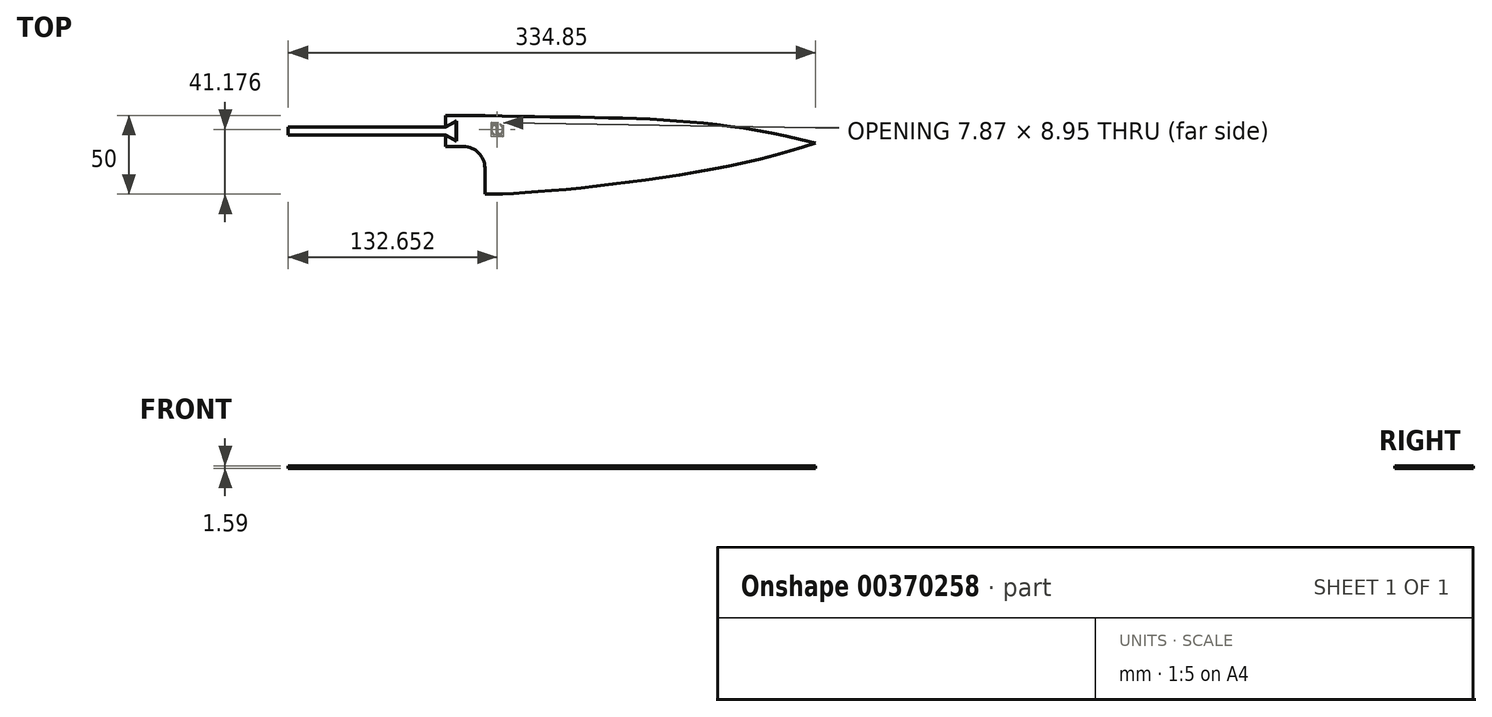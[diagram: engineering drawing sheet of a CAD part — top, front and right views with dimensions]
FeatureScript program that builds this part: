
annotation { "Feature Type Name" : "Feature", "Feature Type Description" : "" }
export const myFeature = defineFeature(function(context is Context, id is Id, definition is map)
    precondition{}
    {
        {
            var Q0;
            Q0=qCreatedBy(makeId("Top.planeOp"),FACE);
            var sketch = newSketch(context, id + "F0", { "sketchPlane" : qUnion([Q0])});
            skLineSegment(sketch, "E0.left", {"start": v(-105, -8.25) * mm, "end": v(-105, -25) * mm});
            skFitSpline(sketch, "E1", {"points": [v(-105, 25) * mm, v(105, 7.62) * mm, v(143.33, 2.67) * mm], "startDerivative": vector(362.44, -9.56) * mm, "endDerivative": vector(-287.35, 150.52) * mm});
            skFitSpline(sketch, "E2", {"points": [v(-105, -25) * mm, v(105, 7.62) * mm], "startDerivative": vector(110.44, 0) * mm, "endDerivative": vector(175.52, 63.31) * mm});
            skArc(sketch, "E3", {"start": v(-105, -8.25) * mm, "mid": v(-108.95, 1.3) * mm, "end": v(-118.5, 5.25) * mm});
            skLineSegment(sketch, "E4", {"start": v(-105, -25) * mm, "end": v(-105, -8.25) * mm});
            skLineSegment(sketch, "E5", {"start": v(-118.5, 5.25) * mm, "end": v(-123.5, 5.25) * mm});
            skLineSegment(sketch, "E6", {"start": v(-105, 25) * mm, "end": v(-123.5, 25) * mm});
            skLineSegment(sketch, "E7.bottom", {"start": v(-123.5, 25) * mm, "end": v(-129.85, 25) * mm});
            skLineSegment(sketch, "E7.top", {"start": v(-123.5, 5.25) * mm, "end": v(-129.85, 5.25) * mm});
            skLineSegment(sketch, "E7.right", {"start": v(-129.85, 25) * mm, "end": v(-129.85, 17.62) * mm});
            skLineSegment(sketch, "E8.bottom", {"start": v(-229.85, 17.62) * mm, "end": v(-129.85, 17.62) * mm});
            skLineSegment(sketch, "E8.top", {"start": v(-229.85, 12.62) * mm, "end": v(-129.85, 12.62) * mm});
            skLineSegment(sketch, "E8.left", {"start": v(-229.85, 17.62) * mm, "end": v(-229.85, 12.62) * mm});
            skLineSegment(sketch, "E9.trimOffspring", {"start": v(-129.85, 12.62) * mm, "end": v(-129.85, 5.25) * mm});
            skSolve(sketch);
        }
        {
            var Q0;
            Q0 = qSketchRegion(id + "F0", true);
            extrude(context, id + "F1", {"entities" : qUnion([Q0]), "depth" : 1.59 * mm});
        }
        {
            var Q0;
            Q0=makeQuery(id+"F1.opExtrude","CAP_FACE",FACE,{"disambiguationData":[OSD([sQuery(id+"F0.wireOp",EDGE,"E1"),sQuery(id+"F0.wireOp",EDGE,"E2"),sQuery(id+"F0.wireOp",EDGE,"E3"),sQuery(id+"F0.wireOp",EDGE,"E4"),sQuery(id+"F0.wireOp",EDGE,"E5"),sQuery(id+"F0.wireOp",EDGE,"E6"),sQuery(id+"F0.wireOp",EDGE,"E7.bottom"),sQuery(id+"F0.wireOp",EDGE,"E7.top"),sQuery(id+"F0.wireOp",EDGE,"E7.right"),sQuery(id+"F0.wireOp",EDGE,"E8.bottom"),sQuery(id+"F0.wireOp",EDGE,"E8.top"),sQuery(id+"F0.wireOp",EDGE,"E8.left"),sQuery(id+"F0.wireOp",EDGE,"E9.trimOffspring")])],"isStart":true});
            var sketch = newSketch(context, id + "F2", { "sketchPlane" : qUnion([Q0])});
            skArc(sketch, "E10", {"start": v(-95.06, -12.8) * mm, "mid": v(-100.52, -13.94) * mm, "end": v(-99.53, -19.43) * mm});
            skArc(sketch, "E11", {"start": v(-95.53, -13.1) * mm, "mid": v(-96.22, -12.82) * mm, "end": v(-96.95, -12.68) * mm});
            skLineSegment(sketch, "E12", {"start": v(-97.45, -12.68) * mm, "end": v(-97.45, -17.8) * mm});
            skLineSegment(sketch, "E13", {"start": v(-96.95, -12.68) * mm, "end": v(-96.95, -13.98) * mm});
            skLineSegment(sketch, "E14", {"start": v(-93.3, -11.7) * mm, "end": v(-94.87, -12.92) * mm});
            skLineSegment(sketch, "E15", {"start": v(-97.45, -17.8) * mm, "end": v(-99.11, -19.1) * mm});
            skPoint(sketch, "E16.orphan", {"position": v(-97.2, -12.18) * mm});
            skLineSegment(sketch, "E17.trimOffspring", {"start": v(-95.06, -12.8) * mm, "end": v(-93.3, -11.7) * mm});
            skLineSegment(sketch, "E18.trimOffspring", {"start": v(-95.28, -13.25) * mm, "end": v(-96.95, -14.56) * mm});
            skLineSegment(sketch, "E19.trimOffspring", {"start": v(-96.95, -14.56) * mm, "end": v(-96.95, -19.67) * mm});
            skLineSegment(sketch, "E20.trimOffspring", {"start": v(-96.95, -13.98) * mm, "end": v(-95.53, -13.1) * mm});
            skArc(sketch, "E21.trimOffspring", {"start": v(-97.45, -12.68) * mm, "mid": v(-100.59, -15.3) * mm, "end": v(-99.11, -19.1) * mm});
            skPoint(sketch, "E22.orphan", {"position": v(-97.2, -14.43) * mm});
            skLineSegment(sketch, "E23.trimOffspring", {"start": v(-97.45, -18.37) * mm, "end": v(-97.45, -19.67) * mm});
            skPoint(sketch, "E24.orphan", {"position": v(-97.2, -17.93) * mm});
            skLineSegment(sketch, "E25.trimOffspring", {"start": v(-97.45, -18.37) * mm, "end": v(-98.86, -19.25) * mm});
            skArc(sketch, "E26.trimOffspring", {"start": v(-96.95, -19.67) * mm, "mid": v(-93.81, -17.06) * mm, "end": v(-95.28, -13.25) * mm});
            skArc(sketch, "E27.trimOffspring", {"start": v(-98.86, -19.25) * mm, "mid": v(-98.18, -19.54) * mm, "end": v(-97.45, -19.67) * mm});
            skArc(sketch, "E28.trimOffspring", {"start": v(-99.34, -19.55) * mm, "mid": v(-93.88, -18.41) * mm, "end": v(-94.87, -12.92) * mm});
            skLineSegment(sketch, "E29.trimOffspring", {"start": v(-99.34, -19.55) * mm, "end": v(-101.09, -20.65) * mm});
            skLineSegment(sketch, "E30.trimOffspring", {"start": v(-99.53, -19.43) * mm, "end": v(-101.09, -20.65) * mm});
            skSolve(sketch);
        }
        {
            var Q0;
            Q0 = qSketchRegion(id + "F2", true);
            extrude(context, id + "F3", {"entities" : qUnion([Q0]), "operationType" : NewBodyOperationType.REMOVE, "oppositeDirection" : true, "offsetDistance" : 25.4 * mm, "depth" : .75 * mm, "hasDraft" : true, "draftAngle" : 20 * degree, "draftPullDirection" : true});
        }
        {
            var Q0;
            Q0=makeQuery(id+"F1.opExtrude","SWEPT_BODY",BODY,{"disambiguationData":[OSD([sQuery(id+"F0.wireOp",EDGE,"E1"),sQuery(id+"F0.wireOp",EDGE,"E2"),sQuery(id+"F0.wireOp",EDGE,"E3"),sQuery(id+"F0.wireOp",EDGE,"E4"),sQuery(id+"F0.wireOp",EDGE,"E5"),sQuery(id+"F0.wireOp",EDGE,"E6"),sQuery(id+"F0.wireOp",EDGE,"E7.bottom"),sQuery(id+"F0.wireOp",EDGE,"E7.top"),sQuery(id+"F0.wireOp",EDGE,"E7.right"),sQuery(id+"F0.wireOp",EDGE,"E8.bottom"),sQuery(id+"F0.wireOp",EDGE,"E8.top"),sQuery(id+"F0.wireOp",EDGE,"E8.left"),sQuery(id+"F0.wireOp",EDGE,"E9.trimOffspring")])]});
            transform(context, id + "F4", {"entities" : qUnion([Q0]), "transformType" : TransformType.TRANSLATION_3D, "dx" : 0 * mm, "dy" : 0 * mm, "dz" : 0 * mm, "makeCopy" : true});
        }
        {
            var Q0;
            {var subQ0=sQuery(id+"F0.wireOp",EDGE,"E8.top");var subQ1=sQuery(id+"F0.wireOp",EDGE,"E8.bottom");var subQ2=sQuery(id+"F0.wireOp",EDGE,"E7.right");var subQ3=sQuery(id+"F0.wireOp",EDGE,"E7.bottom");var subQ4=sQuery(id+"F0.wireOp",EDGE,"E6");var subQ5=sQuery(id+"F0.wireOp",EDGE,"E7.top");var subQ6=sQuery(id+"F0.wireOp",EDGE,"E5");var subQ7=sQuery(id+"F0.wireOp",EDGE,"E8.left");var subQ8=sQuery(id+"F0.wireOp",EDGE,"E1");var subQ9=sQuery(id+"F0.wireOp",EDGE,"E4");var subQ10=sQuery(id+"F0.wireOp",EDGE,"E2");var subQ11=sQuery(id+"F0.wireOp",EDGE,"E3");var subQ12=sQuery(id+"F0.wireOp",EDGE,"E9.trimOffspring");Q0=makeQuery(id+"F4.opPattern","COPY",FACE,{"derivedFrom":makeQuery(id+"F3.boolean.opBoolean","SPLIT",FACE,{"disambiguationData":[TD([makeQuery(id+"F1.opExtrude","SWEPT_FACE",FACE,{"disambiguationData":[OSD([subQ8])]})])],"derivedFrom":makeQuery(id+"F1.opExtrude","CAP_FACE",FACE,{"disambiguationData":[OSD([subQ8,subQ10,subQ11,subQ9,subQ6,subQ4,subQ3,subQ5,subQ2,subQ1,subQ0,subQ7,subQ12])],"isStart":true})}),"instanceName":"1"});}
            var sketch = newSketch(context, id + "F5", { "sketchPlane" : qUnion([Q0])});
            skLineSegment(sketch, "E31", {"start": v(-129.85, -17.62) * mm, "end": v(-123.18, -21.47) * mm});
            skLineSegment(sketch, "E32", {"start": v(-123.18, -21.47) * mm, "end": v(-123.18, -8.77) * mm});
            skLineSegment(sketch, "E33", {"start": v(-123.18, -8.77) * mm, "end": v(-129.85, -12.62) * mm});
            skLineSegment(sketch, "E34.0", {"start": v(-123.12, -8.66) * mm, "end": v(-129.85, -12.55) * mm});
            skLineSegment(sketch, "E34.1", {"start": v(-123.12, -21.58) * mm, "end": v(-123.12, -8.66) * mm});
            skLineSegment(sketch, "E34.2", {"start": v(-129.85, -17.7) * mm, "end": v(-123.12, -21.58) * mm});
            skLineSegment(sketch, "E35", {"start": v(-129.85, -12.62) * mm, "end": v(-129.85, -12.55) * mm});
            skLineSegment(sketch, "E36", {"start": v(-129.85, -17.62) * mm, "end": v(-129.85, -17.7) * mm});
            skSolve(sketch);
        }
        {
            var Q0;
            Q0=makeQuery(id+"F4.opPattern","COPY",FACE,{"derivedFrom":makeQuery(id+"F3.boolean.opBoolean","SPLIT",FACE,{"disambiguationData":[TD([makeQuery(id+"F3.opExtrude","SWEPT_FACE",FACE,{"disambiguationData":[OSD([sQuery(id+"F2.wireOp",EDGE,"E18.trimOffspring")])]})])],"derivedFrom":makeQuery(id+"F1.opExtrude","CAP_FACE",FACE,{"disambiguationData":[OSD([sQuery(id+"F0.wireOp",EDGE,"E1"),sQuery(id+"F0.wireOp",EDGE,"E2"),sQuery(id+"F0.wireOp",EDGE,"E3"),sQuery(id+"F0.wireOp",EDGE,"E4"),sQuery(id+"F0.wireOp",EDGE,"E5"),sQuery(id+"F0.wireOp",EDGE,"E6"),sQuery(id+"F0.wireOp",EDGE,"E7.bottom"),sQuery(id+"F0.wireOp",EDGE,"E7.top"),sQuery(id+"F0.wireOp",EDGE,"E7.right"),sQuery(id+"F0.wireOp",EDGE,"E8.bottom"),sQuery(id+"F0.wireOp",EDGE,"E8.top"),sQuery(id+"F0.wireOp",EDGE,"E8.left"),sQuery(id+"F0.wireOp",EDGE,"E9.trimOffspring")])],"isStart":true})}),"instanceName":"1"});
            var Q1;
            Q1=makeQuery(id+"F4.opPattern","COPY",FACE,{"derivedFrom":makeQuery(id+"F3.boolean.opBoolean","SPLIT",FACE,{"disambiguationData":[TD([makeQuery(id+"F3.opExtrude","SWEPT_FACE",FACE,{"disambiguationData":[OSD([sQuery(id+"F2.wireOp",EDGE,"E25.trimOffspring")])]})])],"derivedFrom":makeQuery(id+"F1.opExtrude","CAP_FACE",FACE,{"disambiguationData":[OSD([sQuery(id+"F0.wireOp",EDGE,"E1"),sQuery(id+"F0.wireOp",EDGE,"E2"),sQuery(id+"F0.wireOp",EDGE,"E3"),sQuery(id+"F0.wireOp",EDGE,"E4"),sQuery(id+"F0.wireOp",EDGE,"E5"),sQuery(id+"F0.wireOp",EDGE,"E6"),sQuery(id+"F0.wireOp",EDGE,"E7.bottom"),sQuery(id+"F0.wireOp",EDGE,"E7.top"),sQuery(id+"F0.wireOp",EDGE,"E7.right"),sQuery(id+"F0.wireOp",EDGE,"E8.bottom"),sQuery(id+"F0.wireOp",EDGE,"E8.top"),sQuery(id+"F0.wireOp",EDGE,"E8.left"),sQuery(id+"F0.wireOp",EDGE,"E9.trimOffspring")])],"isStart":true})}),"instanceName":"1"});
            var Q2;
            Q2=makeQuery(id+"F4.opPattern","COPY",FACE,{"derivedFrom":makeQuery(id+"F3.boolean.opBoolean","SPLIT",FACE,{"disambiguationData":[TD([makeQuery(id+"F3.opExtrude","SWEPT_FACE",FACE,{"disambiguationData":[OSD([sQuery(id+"F2.wireOp",EDGE,"E15")])]})])],"derivedFrom":makeQuery(id+"F1.opExtrude","CAP_FACE",FACE,{"disambiguationData":[OSD([sQuery(id+"F0.wireOp",EDGE,"E1"),sQuery(id+"F0.wireOp",EDGE,"E2"),sQuery(id+"F0.wireOp",EDGE,"E3"),sQuery(id+"F0.wireOp",EDGE,"E4"),sQuery(id+"F0.wireOp",EDGE,"E5"),sQuery(id+"F0.wireOp",EDGE,"E6"),sQuery(id+"F0.wireOp",EDGE,"E7.bottom"),sQuery(id+"F0.wireOp",EDGE,"E7.top"),sQuery(id+"F0.wireOp",EDGE,"E7.right"),sQuery(id+"F0.wireOp",EDGE,"E8.bottom"),sQuery(id+"F0.wireOp",EDGE,"E8.top"),sQuery(id+"F0.wireOp",EDGE,"E8.left"),sQuery(id+"F0.wireOp",EDGE,"E9.trimOffspring")])],"isStart":true})}),"instanceName":"1"});
            var Q3;
            Q3=makeQuery(id+"F4.opPattern","COPY",FACE,{"derivedFrom":makeQuery(id+"F3.boolean.opBoolean","SPLIT",FACE,{"disambiguationData":[TD([makeQuery(id+"F3.opExtrude","SWEPT_FACE",FACE,{"disambiguationData":[OSD([sQuery(id+"F2.wireOp",EDGE,"E13")])]})])],"derivedFrom":makeQuery(id+"F1.opExtrude","CAP_FACE",FACE,{"disambiguationData":[OSD([sQuery(id+"F0.wireOp",EDGE,"E1"),sQuery(id+"F0.wireOp",EDGE,"E2"),sQuery(id+"F0.wireOp",EDGE,"E3"),sQuery(id+"F0.wireOp",EDGE,"E4"),sQuery(id+"F0.wireOp",EDGE,"E5"),sQuery(id+"F0.wireOp",EDGE,"E6"),sQuery(id+"F0.wireOp",EDGE,"E7.bottom"),sQuery(id+"F0.wireOp",EDGE,"E7.top"),sQuery(id+"F0.wireOp",EDGE,"E7.right"),sQuery(id+"F0.wireOp",EDGE,"E8.bottom"),sQuery(id+"F0.wireOp",EDGE,"E8.top"),sQuery(id+"F0.wireOp",EDGE,"E8.left"),sQuery(id+"F0.wireOp",EDGE,"E9.trimOffspring")])],"isStart":true})}),"instanceName":"1"});
            var Q4;
            Q4=makeQuery(id+"F4.opPattern","COPY",EDGE,{"derivedFrom":makeQuery(id+"F3.boolean.opBoolean","COPY",EDGE,{"derivedFrom":makeQuery(id+"F3.opExtrude","CAP_EDGE",EDGE,{"disambiguationData":[OSD([sQuery(id+"F2.wireOp",EDGE,"E28.trimOffspring")])],"isStart":true})}),"instanceName":"1"});
            var Q5;
            Q5=makeQuery(id+"F4.opPattern","COPY",EDGE,{"derivedFrom":makeQuery(id+"F3.boolean.opBoolean","COPY",EDGE,{"derivedFrom":makeQuery(id+"F3.opExtrude","CAP_EDGE",EDGE,{"disambiguationData":[OSD([sQuery(id+"F2.wireOp",EDGE,"E10")])],"isStart":true})}),"instanceName":"1"});
            var Q6;
            Q6=makeQuery(id+"F4.opPattern","COPY",EDGE,{"derivedFrom":makeQuery(id+"F3.boolean.opBoolean","COPY",EDGE,{"derivedFrom":makeQuery(id+"F3.opExtrude","CAP_EDGE",EDGE,{"disambiguationData":[OSD([sQuery(id+"F2.wireOp",EDGE,"E30.trimOffspring")])],"isStart":true})}),"instanceName":"1"});
            var Q7;
            Q7=makeQuery(id+"F4.opPattern","COPY",EDGE,{"derivedFrom":makeQuery(id+"F3.boolean.opBoolean","COPY",EDGE,{"derivedFrom":makeQuery(id+"F3.opExtrude","CAP_EDGE",EDGE,{"disambiguationData":[OSD([sQuery(id+"F2.wireOp",EDGE,"E29.trimOffspring")])],"isStart":true})}),"instanceName":"1"});
            var Q8;
            Q8=makeQuery(id+"F4.opPattern","COPY",EDGE,{"derivedFrom":makeQuery(id+"F3.boolean.opBoolean","COPY",EDGE,{"derivedFrom":makeQuery(id+"F3.opExtrude","CAP_EDGE",EDGE,{"disambiguationData":[OSD([sQuery(id+"F2.wireOp",EDGE,"E14")])],"isStart":true})}),"instanceName":"1"});
            var Q9;
            Q9=makeQuery(id+"F4.opPattern","COPY",EDGE,{"derivedFrom":makeQuery(id+"F3.boolean.opBoolean","COPY",EDGE,{"derivedFrom":makeQuery(id+"F3.opExtrude","CAP_EDGE",EDGE,{"disambiguationData":[OSD([sQuery(id+"F2.wireOp",EDGE,"E17.trimOffspring")])],"isStart":true})}),"instanceName":"1"});
            fillet(context, id + "F6", {"entities" : qUnion([Q0, Q1, Q2, Q3, Q4, Q5, Q6, Q7, Q8, Q9]), "radius" : 0.25 * mm, "tangentPropagation" : true, "allowEdgeOverflow" : false});
        }
        {
            var Q0;
            Q0 = qSketchRegion(id + "F5", true);
            extrude(context, id + "F7", {"entities" : qUnion([Q0]), "operationType" : NewBodyOperationType.REMOVE, "oppositeDirection" : true, "depth" : 25.4 * mm});
        }
    });
